# Revit family: QF_ELECTROLUXPROFESSIONAL_1LSNTN_WN6-20_S
name_source: partatom
category: Attrezzature speciali
units: mm (PartAtom-declared; Revit-internal decimal feet)

## family parameters
Basato su piano di lavoro = No
Condiviso = No
Punto di calcolo locali = No
Quota connettore circolare = Usa diametro
Sempre verticale = Sì
Taglio con vuoti quando caricato = No
Tipo di parte = Normale

## types (4) — shared parameters
Depth = 915.5 mm  [stored 3.00361 ft]
Depth Actual = 915 mm  [stored 3.00197 ft]
Height = 1346.8 mm  [stored 4.41864 ft]
Height Actual = 1345 mm
Latent Heat Output = 0.0
Length Actual = 750 mm  [stored 2.46063 ft]
Modello = WN6-20
Produttore = Electrolux Professional
Sensible Heat Output = 0.0
URL = www.electroluxprofessional.com
Weight = 207
Width = 750 mm  [stored 2.46063 ft]
zero-valued in all types: Gas KW, Prospetto di default, Steam Pounds per Hour

## per-type parameters (varying)
| type | Cycle | Descrizione | Item Number | Phase | Volts | Watts |
| 9867830146 | 50 Hz | WASHER WN6-20 20KG STEAM 220-240/50/1N COMPASS PRO 6G01 ML 2xWATER POWDER+5xLIQ. VALV.OPEN SILVER 2.I/O DISCON. STOP | 1L0GD2 | 1 | 240 V | 800 W |
| 9867830219 | 60 Hz | WASHER WN6-20 20KG STEAM 220-240/60/1N COMPASS PRO 6G01 ML 2xWATER POWDER+5xLIQ. VALV.OPEN SILVER 2.I/O DISCON. STOP | 1LSPLE | 1 | 240 V | 800 W |
| 9867830273 | 50 Hz | WASHER WN6-20 20KG STEAM 220-240/50/1N COMPASS PRO 6G01 ML 2xWATER POWDER+5xLIQ. EL.VALV.OPEN SST 2.I/O DISCON. STOP | 1L0HD3 | 1 | 240 V | 800 W |
| 9867830151 | 50 Hz | WASHER WN6-20 20KG STEAM 200/50/60/3 COMPASS PRO 6G41 JP,EN 2xWATER POWDER+5xLIQ. VALV.OPEN SST/SILVER SL.DRUM 2.I/O DIS | 1LA1AJ | 3 | 200 V | 1500 W |

note: [stored X ft] marks values corroborated as IEEE doubles in the binary element streams (Revit-internal decimal feet)

## geometry (parser evidence)
native form markers: Sweep x5
no freeform markers — native parametric forms only
